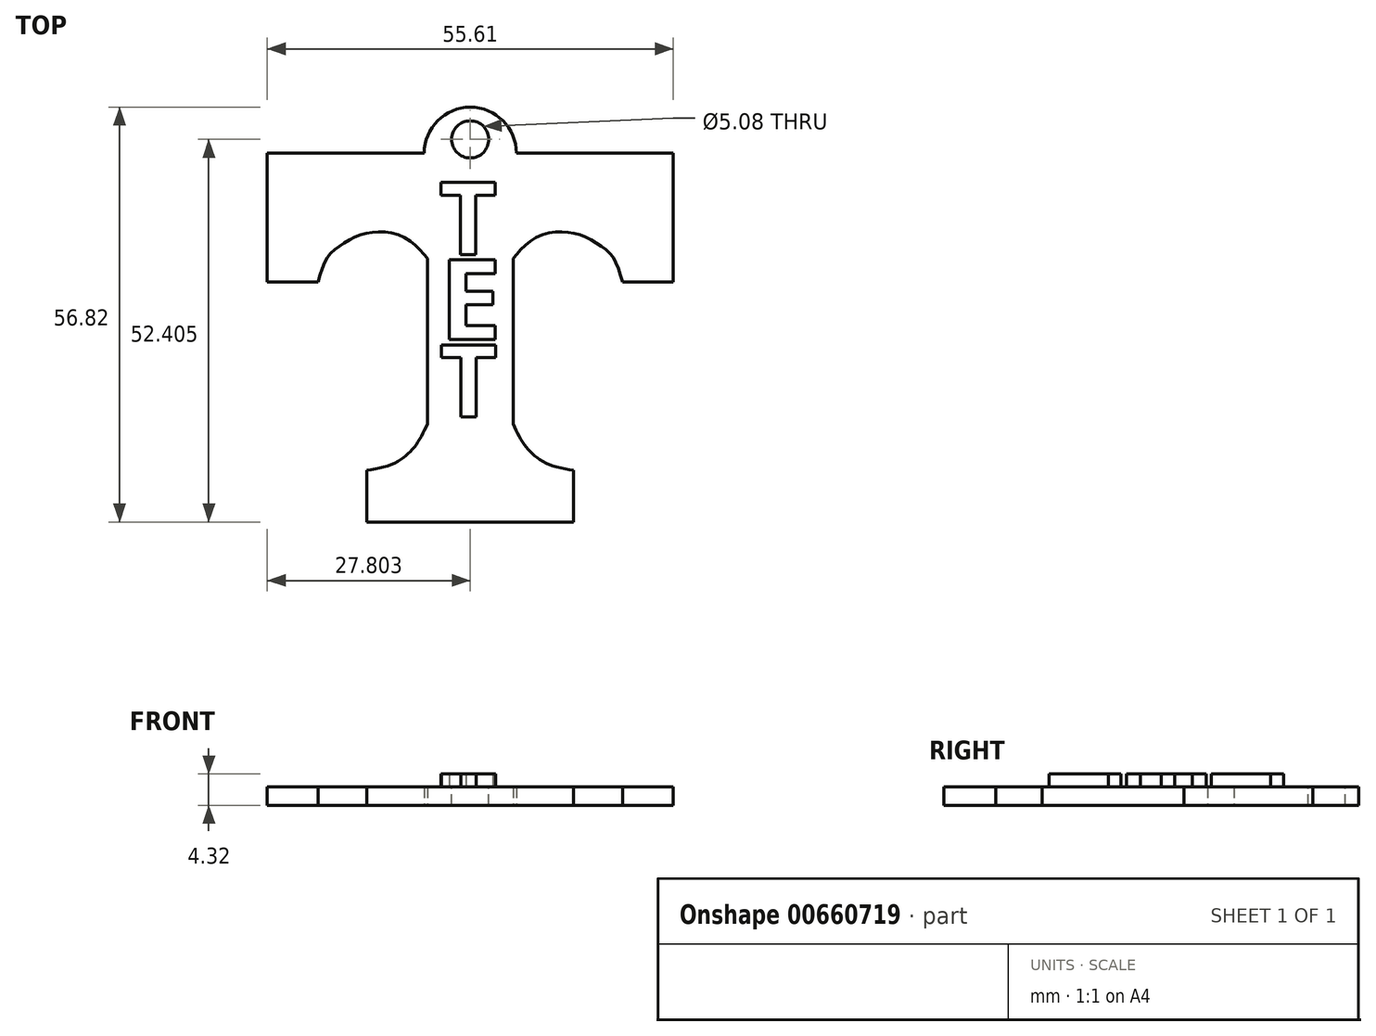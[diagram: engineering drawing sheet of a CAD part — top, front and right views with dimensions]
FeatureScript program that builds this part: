
annotation { "Feature Type Name" : "Feature", "Feature Type Description" : "" }
export const myFeature = defineFeature(function(context is Context, id is Id, definition is map)
    precondition{}
    {
        {
            var Q0;
            Q0=qCreatedBy(makeId("Top.planeOp"),FACE);
            var sketch = newSketch(context, id + "F0", { "sketchPlane" : qUnion([Q0])});
            skLineSegment(sketch, "E0", {"start": v(1.3, -2.36) * mm, "end": v(22.8, -2.36) * mm});
            skLineSegment(sketch, "E1", {"start": v(56.9, -2.36) * mm, "end": v(56.9, -19.98) * mm});
            skLineSegment(sketch, "E2", {"start": v(56.9, -19.98) * mm, "end": v(49.97, -19.98) * mm});
            skLineSegment(sketch, "E3", {"start": v(1.3, -2.36) * mm, "end": v(1.3, -19.98) * mm});
            skLineSegment(sketch, "E4", {"start": v(23.12, -16.78) * mm, "end": v(23.12, -39.28) * mm});
            skLineSegment(sketch, "E5", {"start": v(34.97, -16.78) * mm, "end": v(34.97, -39.43) * mm});
            skLineSegment(sketch, "E6", {"start": v(14.94, -52.87) * mm, "end": v(43.27, -52.87) * mm});
            skLineSegment(sketch, "E7", {"start": v(43.27, -52.87) * mm, "end": v(43.27, -45.8) * mm});
            skFitSpline(sketch, "E8", {"points": [v(34.97, -16.78) * mm, v(36.26, -15.33) * mm, v(38.25, -13.85) * mm, v(40.76, -13.14) * mm, v(42.94, -13.27) * mm, v(44.94, -13.85) * mm, v(46.74, -14.88) * mm, v(48.15, -15.97) * mm, v(49.12, -17.51) * mm, v(49.97, -19.98) * mm], "startDerivative": vector(11.36, 13.8) * mm, "endDerivative": vector(6.55, -21.4) * mm});
            skFitSpline(sketch, "E9", {"points": [v(34.97, -39.43) * mm, v(35.94, -41.36) * mm, v(36.97, -42.84) * mm, v(38.19, -44) * mm, v(40.18, -45.1) * mm, v(43.27, -45.8) * mm], "startDerivative": vector(4.69, -10.05) * mm, "endDerivative": vector(13.5, -2.31) * mm});
            skFitSpline(sketch, "E10.MirrorCS", {"points": [v(23.23, -16.78) * mm, v(21.95, -15.33) * mm, v(19.95, -13.85) * mm, v(17.45, -13.14) * mm, v(15.26, -13.27) * mm, v(13.27, -13.85) * mm, v(11.47, -14.88) * mm, v(10.05, -15.97) * mm, v(9.09, -17.51) * mm, v(8.24, -19.98) * mm], "startDerivative": vector(-11.36, 13.8) * mm, "endDerivative": vector(-6.55, -21.4) * mm});
            skFitSpline(sketch, "E11.MirrorCS", {"points": [v(23.23, -39.43) * mm, v(22.27, -41.36) * mm, v(21.24, -42.84) * mm, v(20.02, -44) * mm, v(18.03, -45.1) * mm, v(14.94, -45.8) * mm], "startDerivative": vector(-4.69, -10.05) * mm, "endDerivative": vector(-13.5, -2.31) * mm});
            skLineSegment(sketch, "E12.MirrorCS", {"start": v(1.3, -19.98) * mm, "end": v(8.24, -19.98) * mm});
            skLineSegment(sketch, "E13.MirrorCS", {"start": v(14.94, -52.87) * mm, "end": v(14.94, -45.8) * mm});
            skLineSegment(sketch, "E14.MirrorCS", {"start": v(23.23, -16.78) * mm, "end": v(23.23, -39.43) * mm});
            skPoint(sketch, "E15.start.orphan", {"position": v(29.1, -2.36) * mm});
            skArc(sketch, "E16", {"start": v(35.41, -2.36) * mm, "mid": v(29.1, 3.95) * mm, "end": v(22.8, -2.36) * mm});
            skLineSegment(sketch, "E17.trimOffspring", {"start": v(35.41, -2.36) * mm, "end": v(56.9, -2.36) * mm});
            skSolve(sketch);
        }
        {
            var Q0;
            Q0=makeQuery(id+"F0.imprint","IMPRINT",FACE,{"disambiguationData":[TD([[makeQuery(id+"F0.imprint","IMPRINT",EDGE,{"derivedFrom":sQuery(id+"F0.wireOp",EDGE,"E0")}),-1.0]])]});
            extrude(context, id + "F1", {"entities" : qUnion([Q0]), "depth" : 2.54 * mm, "offsetDistance" : 25.4 * mm});
        }
        {
            var Q0;
            Q0=makeQuery(id+"F1.opExtrude","CAP_FACE",FACE,{"disambiguationData":[OSD([sQuery(id+"F0.wireOp",EDGE,"E0"),sQuery(id+"F0.wireOp",EDGE,"E1"),sQuery(id+"F0.wireOp",EDGE,"E2"),sQuery(id+"F0.wireOp",EDGE,"E5"),sQuery(id+"F0.wireOp",EDGE,"E6"),sQuery(id+"F0.wireOp",EDGE,"E7"),sQuery(id+"F0.wireOp",EDGE,"E8"),sQuery(id+"F0.wireOp",EDGE,"E9"),sQuery(id+"F0.wireOp",EDGE,"E10.MirrorCS"),sQuery(id+"F0.wireOp",EDGE,"E11.MirrorCS"),sQuery(id+"F0.wireOp",EDGE,"E12.MirrorCS"),sQuery(id+"F0.wireOp",EDGE,"E3"),sQuery(id+"F0.wireOp",EDGE,"E13.MirrorCS"),sQuery(id+"F0.wireOp",EDGE,"E14.MirrorCS"),sQuery(id+"F0.wireOp",EDGE,"E16"),sQuery(id+"F0.wireOp",EDGE,"E17.trimOffspring")])],"isStart":false});
            var sketch = newSketch(context, id + "F2", { "sketchPlane" : qUnion([Q0])});
            skCircle(sketch, "E18", {"center": v(29.1, -0.46) * mm, "radius": 2.32 * mm});
            skPoint(sketch, "E19.orphan", {"position": v(29.1, 3.95) * mm});
            skPoint(sketch, "E20.start.orphan", {"position": v(29.1, -2.36) * mm});
            skPoint(sketch, "E21.trimOffspring.end.orphan", {"position": v(35.41, -2.36) * mm});
            skPoint(sketch, "E22.start.orphan", {"position": v(22.8, -2.36) * mm});
            skSolve(sketch);
        }
        {
            var Q0;
            Q0=sQuery(id+"F2.wireOp",VERTEX,"E18.center");
            var Q1;
            Q1=makeQuery(id+"F1.opExtrude","SWEPT_BODY",BODY,{"disambiguationData":[OSD([sQuery(id+"F0.wireOp",EDGE,"E0"),sQuery(id+"F0.wireOp",EDGE,"E1"),sQuery(id+"F0.wireOp",EDGE,"E2"),sQuery(id+"F0.wireOp",EDGE,"E5"),sQuery(id+"F0.wireOp",EDGE,"E6"),sQuery(id+"F0.wireOp",EDGE,"E7"),sQuery(id+"F0.wireOp",EDGE,"E8"),sQuery(id+"F0.wireOp",EDGE,"E9"),sQuery(id+"F0.wireOp",EDGE,"E10.MirrorCS"),sQuery(id+"F0.wireOp",EDGE,"E11.MirrorCS"),sQuery(id+"F0.wireOp",EDGE,"E12.MirrorCS"),sQuery(id+"F0.wireOp",EDGE,"E3"),sQuery(id+"F0.wireOp",EDGE,"E13.MirrorCS"),sQuery(id+"F0.wireOp",EDGE,"E14.MirrorCS"),sQuery(id+"F0.wireOp",EDGE,"E16"),sQuery(id+"F0.wireOp",EDGE,"E17.trimOffspring")])]});
            hole(context, id + "F3", {"style" : HoleStyle.SIMPLE, "endStyle" : HoleEndStyle.THROUGH, "holeDiameter" : 5.08 * mm, "majorDiameter" : 6.35 * mm, "isTappedThrough" : true, "tappedDepth" : 12.7 * mm, "tapClearance" : 3, "locations" : qUnion([Q0]), "scope" : qUnion([Q1])});
        }
        {
            var Q0;
            Q0=makeQuery(id+"F1.opExtrude","CAP_FACE",FACE,{"disambiguationData":[OSD([sQuery(id+"F0.wireOp",EDGE,"E0"),sQuery(id+"F0.wireOp",EDGE,"E1"),sQuery(id+"F0.wireOp",EDGE,"E2"),sQuery(id+"F0.wireOp",EDGE,"E5"),sQuery(id+"F0.wireOp",EDGE,"E6"),sQuery(id+"F0.wireOp",EDGE,"E7"),sQuery(id+"F0.wireOp",EDGE,"E8"),sQuery(id+"F0.wireOp",EDGE,"E9"),sQuery(id+"F0.wireOp",EDGE,"E10.MirrorCS"),sQuery(id+"F0.wireOp",EDGE,"E11.MirrorCS"),sQuery(id+"F0.wireOp",EDGE,"E12.MirrorCS"),sQuery(id+"F0.wireOp",EDGE,"E3"),sQuery(id+"F0.wireOp",EDGE,"E13.MirrorCS"),sQuery(id+"F0.wireOp",EDGE,"E14.MirrorCS"),sQuery(id+"F0.wireOp",EDGE,"E16"),sQuery(id+"F0.wireOp",EDGE,"E17.trimOffspring")])],"isStart":false});
            var sketch = newSketch(context, id + "F4", { "sketchPlane" : qUnion([Q0])});
            skPoint(sketch, "E23.secondSnap0", {"position": v(46.16, -2.36) * mm});
            skText(sketch, "E24", { "text": "T", "fontName": "OpenSans-Bold.ttf"});
            skText(sketch, "E25", { "text": "E", "fontName": "OpenSans-Bold.ttf"});
            skText(sketch, "E26", { "text": "T", "fontName": "OpenSans-Bold.ttf"});
            const initialGuessF4  = {"E24": [0.02479, -0.01623, 1, 0, 0.00995], "E25": [0.02485, -0.02785, 1, 0, 0.01097], "E26": [0.02485, -0.03849, 1, 0, 0.00995]};
            skSetInitialGuess(sketch, initialGuessF4);
            skSolve(sketch);
        }
        {
            var Q0;
            Q0=makeQuery(id+"F4.imprint","IMPRINT",FACE,{"disambiguationData":[TD([[makeQuery(id+"F4.imprint","IMPRINT",EDGE,{"derivedFrom":sQuery(id+"F4.wireOp",EDGE,"E24.sketch_text.stroke-0")}),-1.0]])]});
            var Q1;
            Q1=makeQuery(id+"F4.imprint","IMPRINT",FACE,{"disambiguationData":[TD([[makeQuery(id+"F4.imprint","IMPRINT",EDGE,{"derivedFrom":sQuery(id+"F4.wireOp",EDGE,"E25.sketch_text.stroke-0")}),-1.0]])]});
            var Q2;
            Q2=makeQuery(id+"F4.imprint","IMPRINT",FACE,{"disambiguationData":[TD([[makeQuery(id+"F4.imprint","IMPRINT",EDGE,{"derivedFrom":sQuery(id+"F4.wireOp",EDGE,"E26.sketch_text.stroke-0")}),-1.0]])]});
            extrude(context, id + "F5", {"entities" : qUnion([Q0, Q1, Q2]), "operationType" : NewBodyOperationType.ADD, "depth" : 1.78 * mm, "offsetDistance" : 25.4 * mm});
        }
    });
